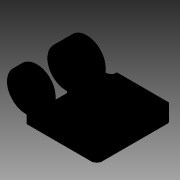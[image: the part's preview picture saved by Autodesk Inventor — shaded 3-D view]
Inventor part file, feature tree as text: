
AUTODESK INVENTOR PART (.ipt)
format: ipt  version: 2014 SP2 (Build 180246200, 246)  size: 205,824 bytes
history: native  units: in
note: dims shown in document units (in); Inventor stores cm internally (conversion verified against a paired STEP export)
features: sketch x9, extrude x7, other x7, revolve x2
ambient origin geometry x8: Origin, YZ Plane, XZ Plane, XY Plane, X Axis, Y Axis, Z Axis, Center Point
bodies: Solid1 (feature_tree)
feature tree (25):
  extrude  "Extrusion1"  Depth=1.5748in TaperAngle=0.0deg
  extrude  "Extrusion2"  Depth=1.5748in TaperAngle=0.0deg
  extrude  "Extrusion3"  TaperAngle=360.0deg  [1 undecoded]
  extrude  "Extrusion4"  TaperAngle=360.0deg  [1 undecoded]
  extrude  "Extrusion5"  [1 undecoded]
  revolve  "Revolution1"  [1 undecoded]
  extrude  "Extrusion6"  [1 undecoded]
  revolve  "Revolution2"  [1 undecoded]
  extrude  "Extrusion7"  [1 undecoded]
  other  "to_a_XY"
  other  "to_a_YZ"
  other  "to_a_ZX"
  other  "to_a_X"
  other  "to_a_Y"
  other  "to_a_Z"
  other  "to_a_Center"
  sketch  "Sketch_1"  dims[d0=0.312in d1=0.0in d2=1.5748in d3=0.0in]
  sketch  "Sketch_2"  dims[d4=2.9134in d5=0.0in d6=1.5748in d7=0.0in]
  sketch  "Sketch_3"  dims[d8=0.462in d9=0.0in d10=360.0deg]
  sketch  "Sketch_4"  dims[d11=0.462in d12=0.0in d13=360.0deg]
  sketch  "Sketch_5"  dims[d14=1.5748in d15=0.0in]
  sketch  "Sketch_6"
  sketch  "Sketch_7"
  sketch  "Sketch_8"
  sketch  "Sketch_9"
note: 7 required parameter values undecoded (feature->parameter linkage not recoverable at this tier; creation-order binding heuristic only, values carry confidence <= 0.55)
